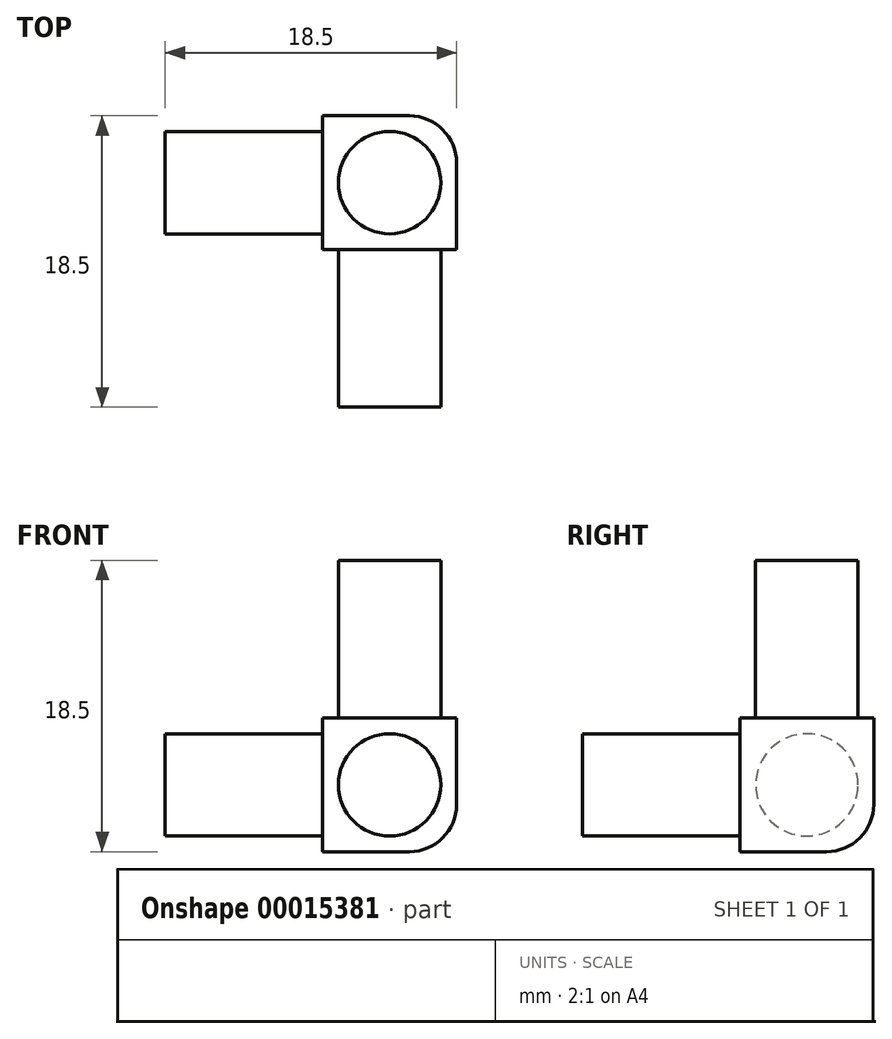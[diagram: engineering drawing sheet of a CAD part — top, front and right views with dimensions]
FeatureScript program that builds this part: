
annotation { "Feature Type Name" : "Feature", "Feature Type Description" : "" }
export const myFeature = defineFeature(function(context is Context, id is Id, definition is map)
    precondition{}
    {
        {
            var Q0;
            Q0=qCreatedBy(makeId("Top.planeOp"),FACE);
            var sketch = newSketch(context, id + "F0", { "sketchPlane" : qUnion([Q0])});
            skCircle(sketch, "E0", {"center": v(0, 0) * mm, "radius": 3.25 * mm});
            skSolve(sketch);
        }
        {
            var Q0;
            Q0=makeQuery(id+"F0.imprint","IMPRINT",FACE,{"disambiguationData":[TD([[makeQuery(id+"F0.imprint","IMPRINT",EDGE,{"derivedFrom":sQuery(id+"F0.wireOp",EDGE,"E0")}),1.0]])]});
            extrude(context, id + "F1", {"entities" : qUnion([Q0]), "depth" : 10 * mm});
        }
        {
            var Q0;
            Q0=makeQuery(id+"F1.opExtrude","CAP_FACE",FACE,{"disambiguationData":[OSD([sQuery(id+"F0.wireOp",EDGE,"E0")])],"isStart":true});
            var sketch = newSketch(context, id + "F2", { "sketchPlane" : qUnion([Q0])});
            skLineSegment(sketch, "E1.bottom", {"start": v(-4.25, 4.25) * mm, "end": v(4.25, 4.25) * mm});
            skLineSegment(sketch, "E1.top", {"start": v(-4.25, -4.25) * mm, "end": v(4.25, -4.25) * mm});
            skLineSegment(sketch, "E1.left", {"start": v(-4.25, 4.25) * mm, "end": v(-4.25, -4.25) * mm});
            skLineSegment(sketch, "E1.right", {"start": v(4.25, 4.25) * mm, "end": v(4.25, -4.25) * mm});
            skSolve(sketch);
        }
        {
            var Q0;
            Q0=qSketchRegion(id+"F2",true);
            extrude(context, id + "F3", {"entities" : qUnion([Q0]), "operationType" : NewBodyOperationType.ADD, "depth" : 8.5 * mm});
        }
        {
            var Q0;
            Q0=makeQuery(id+"F3.opExtrude","SWEPT_FACE",FACE,{"disambiguationData":[OSD([sQuery(id+"F2.wireOp",EDGE,"E1.left")])]});
            var sketch = newSketch(context, id + "F4", { "sketchPlane" : qUnion([Q0])});
            skCircle(sketch, "E2", {"center": v(0, -4.25) * mm, "radius": 3.25 * mm});
            skSolve(sketch);
        }
        {
            var Q0;
            Q0=qSketchRegion(id+"F4",true);
            var Q1;
            Q1=qConstructionFilter(qBodyType(qCreatedBy(id+"F4",EDGE),BodyType.WIRE),ConstructionObject.NO);
            extrude(context, id + "F5", {"entities" : qUnion([Q0]), "operationType" : NewBodyOperationType.ADD, "surfaceEntities" : qUnion([Q1]), "depth" : 10 * mm});
        }
        {
            var Q0;
            Q0=makeQuery(id+"F3.opExtrude","SWEPT_FACE",FACE,{"disambiguationData":[OSD([sQuery(id+"F2.wireOp",EDGE,"E1.bottom")])]});
            var sketch = newSketch(context, id + "F6", { "sketchPlane" : qUnion([Q0])});
            skCircle(sketch, "E3", {"center": v(0, -4.25) * mm, "radius": 3.25 * mm});
            skSolve(sketch);
        }
        {
            var Q0;
            Q0=qSketchRegion(id+"F6",true);
            extrude(context, id + "F7", {"entities" : qUnion([Q0]), "operationType" : NewBodyOperationType.ADD, "depth" : 10 * mm});
        }
        {
            var Q0;
            Q0=makeQuery(id+"F3.opExtrude","SWEPT_EDGE",EDGE,{"disambiguationData":[OSD([sQuery(id+"F2.wireOp",EDGE,"E1.top"),sQuery(id+"F2.wireOp",EDGE,"E1.right")])]});
            var Q1;
            Q1=makeQuery(id+"F3.opExtrude","CAP_EDGE",EDGE,{"disambiguationData":[OSD([sQuery(id+"F2.wireOp",EDGE,"E1.right")])],"isStart":false});
            var Q2;
            Q2=makeQuery(id+"F3.opExtrude","CAP_EDGE",EDGE,{"disambiguationData":[OSD([sQuery(id+"F2.wireOp",EDGE,"E1.top")])],"isStart":false});
            fillet(context, id + "F8", {"entities" : qUnion([Q0, Q1, Q2]), "radius" : 3 * mm, "tangentPropagation" : true, "allowEdgeOverflow" : false});
        }
    });
